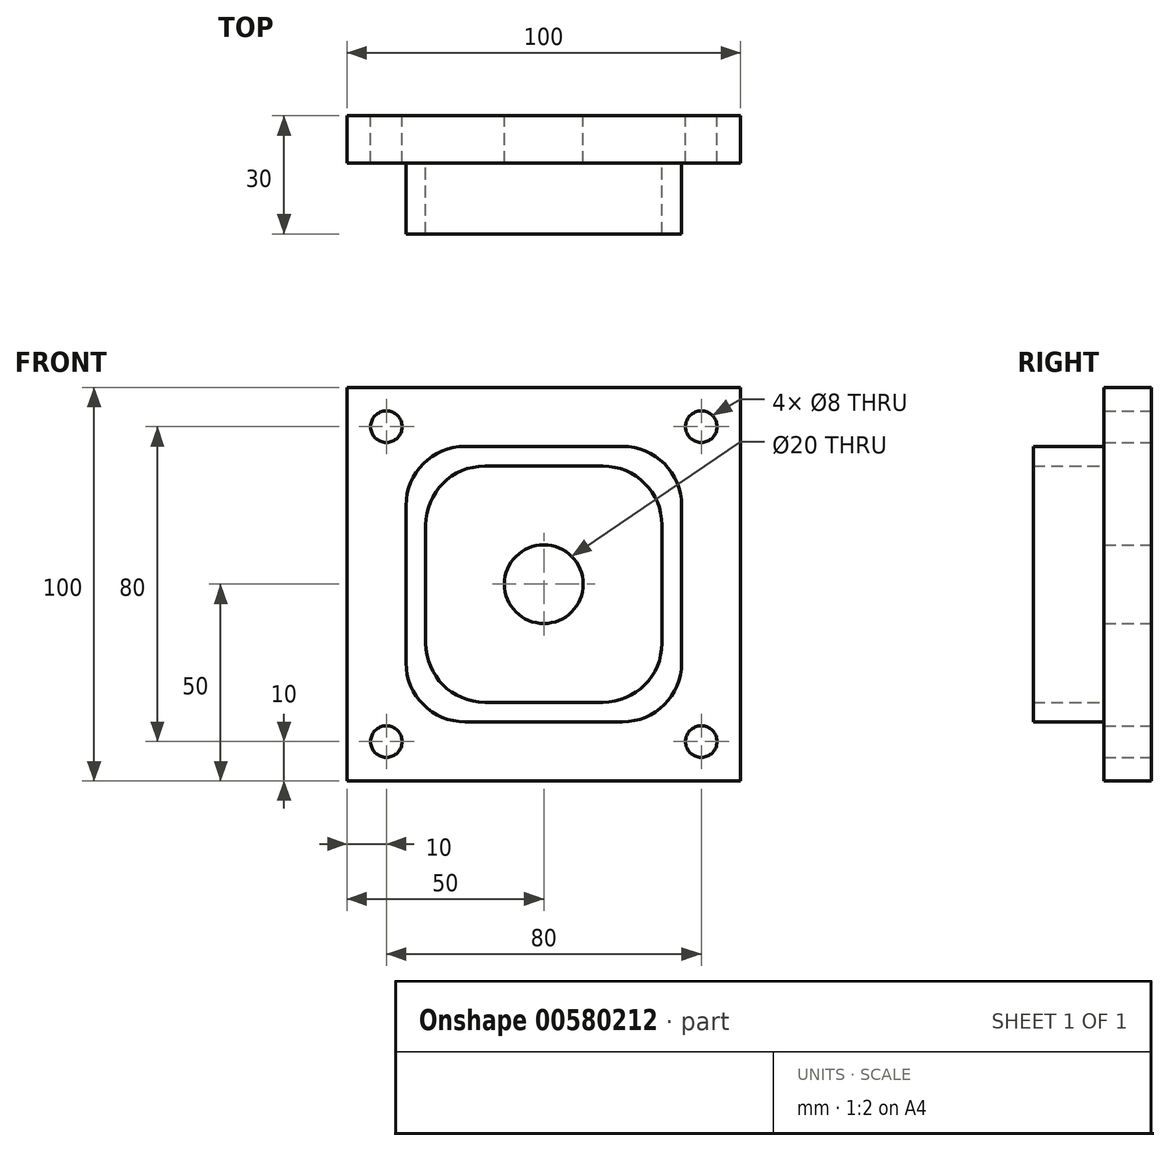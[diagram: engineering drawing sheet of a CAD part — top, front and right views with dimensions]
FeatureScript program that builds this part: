
annotation { "Feature Type Name" : "Feature", "Feature Type Description" : "" }
export const myFeature = defineFeature(function(context is Context, id is Id, definition is map)
    precondition{}
    {
        {
            var Q0;
            Q0=qCreatedBy(makeId("Front.planeOp"),FACE);
            var sketch = newSketch(context, id + "F0", { "sketchPlane" : qUnion([Q0])});
            skLineSegment(sketch, "E0", {"start": v(0, 0) * mm, "end": v(-100, 0) * mm});
            skLineSegment(sketch, "E1", {"start": v(-100, 0) * mm, "end": v(-100, 100) * mm});
            skLineSegment(sketch, "E2", {"start": v(-100, 100) * mm, "end": v(0, 100) * mm});
            skLineSegment(sketch, "E3", {"start": v(0, 100) * mm, "end": v(0, 0) * mm});
            skLineSegment(sketch, "E4.bottom", {"start": v(-90, 90) * mm, "end": v(-10, 90) * mm, "construction": true});
            skLineSegment(sketch, "E4.top", {"start": v(-90, 10) * mm, "end": v(-10, 10) * mm, "construction": true});
            skLineSegment(sketch, "E4.left", {"start": v(-90, 90) * mm, "end": v(-90, 10) * mm, "construction": true});
            skLineSegment(sketch, "E4.right", {"start": v(-10, 90) * mm, "end": v(-10, 10) * mm, "construction": true});
            skCircle(sketch, "E5", {"center": v(-10, 90) * mm, "radius": 4 * mm});
            skCircle(sketch, "E6", {"center": v(-10, 10) * mm, "radius": 4 * mm});
            skCircle(sketch, "E7", {"center": v(-90, 10) * mm, "radius": 4 * mm});
            skCircle(sketch, "E8", {"center": v(-90, 90) * mm, "radius": 4 * mm});
            skLineSegment(sketch, "E9.bottom", {"start": v(-70, 85) * mm, "end": v(-30, 85) * mm});
            skLineSegment(sketch, "E9.top", {"start": v(-70, 15) * mm, "end": v(-30, 15) * mm});
            skLineSegment(sketch, "E9.left", {"start": v(-85, 70) * mm, "end": v(-85, 30) * mm});
            skLineSegment(sketch, "E9.right", {"start": v(-15, 70) * mm, "end": v(-15, 30) * mm});
            skLineSegment(sketch, "E10.bottom", {"start": v(-65, 80) * mm, "end": v(-35, 80) * mm});
            skLineSegment(sketch, "E10.top", {"start": v(-65, 20) * mm, "end": v(-35, 20) * mm});
            skLineSegment(sketch, "E10.left", {"start": v(-80, 65) * mm, "end": v(-80, 35) * mm});
            skLineSegment(sketch, "E10.right", {"start": v(-20, 65) * mm, "end": v(-20, 35) * mm});
            skPoint(sketch, "E11.visualSharp", {"position": v(-85, 85) * mm});
            skArc(sketch, "E11.filletArc", {"start": v(-70, 85) * mm, "mid": v(-80.6, 80.6) * mm, "end": v(-85, 70) * mm});
            skPoint(sketch, "E12.visualSharp", {"position": v(-15, 85) * mm});
            skArc(sketch, "E12.filletArc", {"start": v(-15, 70) * mm, "mid": v(-19.4, 80.6) * mm, "end": v(-30, 85) * mm});
            skPoint(sketch, "E13.visualSharp", {"position": v(-15, 15) * mm});
            skArc(sketch, "E13.filletArc", {"start": v(-30, 15) * mm, "mid": v(-19.4, 19.4) * mm, "end": v(-15, 30) * mm});
            skPoint(sketch, "E14.visualSharp", {"position": v(-80, 80) * mm});
            skArc(sketch, "E14.filletArc", {"start": v(-65, 80) * mm, "mid": v(-75.6, 75.6) * mm, "end": v(-80, 65) * mm});
            skPoint(sketch, "E15.visualSharp", {"position": v(-20, 80) * mm});
            skArc(sketch, "E15.filletArc", {"start": v(-20, 65) * mm, "mid": v(-24.4, 75.6) * mm, "end": v(-35, 80) * mm});
            skPoint(sketch, "E16.visualSharp", {"position": v(-80, 20) * mm});
            skArc(sketch, "E16.filletArc", {"start": v(-80, 35) * mm, "mid": v(-75.6, 24.4) * mm, "end": v(-65, 20) * mm});
            skPoint(sketch, "E17.visualSharp", {"position": v(-20, 20) * mm});
            skArc(sketch, "E17.filletArc", {"start": v(-35, 20) * mm, "mid": v(-24.4, 24.4) * mm, "end": v(-20, 35) * mm});
            skPoint(sketch, "E18.visualSharp", {"position": v(-85, 15) * mm});
            skArc(sketch, "E18.filletArc", {"start": v(-85, 30) * mm, "mid": v(-80.6, 19.4) * mm, "end": v(-70, 15) * mm});
            skCircle(sketch, "E19", {"center": v(-50, 50) * mm, "radius": 10 * mm});
            skLineSegment(sketch, "E20", {"start": v(-65, 65) * mm, "end": v(-35, 35) * mm, "construction": true});
            skLineSegment(sketch, "E21", {"start": v(-65, 35) * mm, "end": v(-35, 65) * mm, "construction": true});
            skSolve(sketch);
        }
        {
            var Q0;
            Q0=makeQuery(id+"F0.imprint","IMPRINT",FACE,{"disambiguationData":[TD([[makeQuery(id+"F0.imprint","IMPRINT",EDGE,{"derivedFrom":sQuery(id+"F0.wireOp",EDGE,"E9.bottom")}),-1.0]])]});
            extrude(context, id + "F1", {"entities" : qUnion([Q0]), "depth" : 30 * mm, "offsetDistance" : 25 * mm});
        }
        {
            var Q0;
            Q0=makeQuery(id+"F0.imprint","IMPRINT",FACE,{"disambiguationData":[TD([[makeQuery(id+"F0.imprint","IMPRINT",EDGE,{"derivedFrom":sQuery(id+"F0.wireOp",EDGE,"E0")}),-1.0]])]});
            var Q1;
            Q1=makeQuery(id+"F0.imprint","IMPRINT",FACE,{"disambiguationData":[TD([[makeQuery(id+"F0.imprint","IMPRINT",EDGE,{"derivedFrom":sQuery(id+"F0.wireOp",EDGE,"E10.bottom")}),-1.0]])]});
            extrude(context, id + "F2", {"entities" : qUnion([Q0, Q1]), "operationType" : NewBodyOperationType.ADD, "depth" : 12 * mm, "offsetDistance" : 25 * mm});
        }
    });
